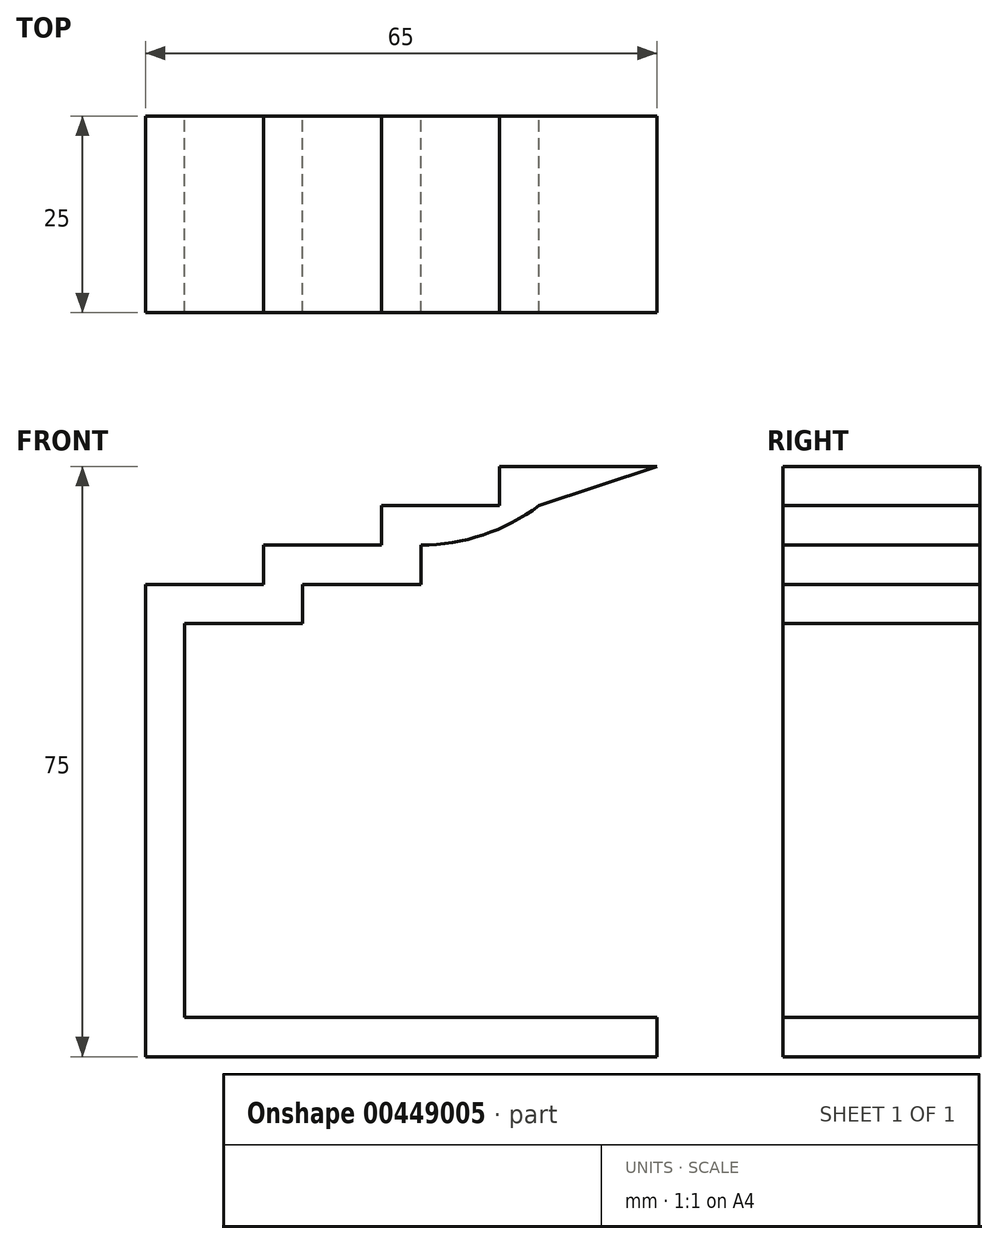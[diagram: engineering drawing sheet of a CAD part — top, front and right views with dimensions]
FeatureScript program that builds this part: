
annotation { "Feature Type Name" : "Feature", "Feature Type Description" : "" }
export const myFeature = defineFeature(function(context is Context, id is Id, definition is map)
    precondition{}
    {
        {
            var Q0;
            Q0=qCreatedBy(makeId("Front.planeOp"),FACE);
            var sketch = newSketch(context, id + "F0", { "sketchPlane" : qUnion([Q0])});
            skLineSegment(sketch, "E0.bottom", {"start": v(0, 0) * mm, "end": v(65, 0) * mm});
            skLineSegment(sketch, "E0.top", {"start": v(0, 5) * mm, "end": v(65, 5) * mm});
            skLineSegment(sketch, "E0.left", {"start": v(0, 0) * mm, "end": v(0, 5) * mm});
            skLineSegment(sketch, "E0.right", {"start": v(65, 0) * mm, "end": v(65, 5) * mm});
            skLineSegment(sketch, "E1.bottom", {"start": v(0, 5) * mm, "end": v(5, 5) * mm});
            skLineSegment(sketch, "E1.top", {"start": v(0, 55) * mm, "end": v(5, 55) * mm});
            skLineSegment(sketch, "E1.left", {"start": v(0, 5) * mm, "end": v(0, 55) * mm});
            skLineSegment(sketch, "E1.right", {"start": v(5, 5) * mm, "end": v(5, 55) * mm});
            skLineSegment(sketch, "E2", {"start": v(0, 55) * mm, "end": v(20, 55) * mm});
            skLineSegment(sketch, "E3", {"start": v(20, 55) * mm, "end": v(20, 60) * mm});
            skLineSegment(sketch, "E4", {"start": v(20, 60) * mm, "end": v(35, 60) * mm});
            skLineSegment(sketch, "E5", {"start": v(35, 60) * mm, "end": v(35, 65) * mm});
            skLineSegment(sketch, "E6", {"start": v(35, 65) * mm, "end": v(50, 65) * mm, "construction": true});
            skLineSegment(sketch, "E7", {"start": v(50, 65) * mm, "end": v(50, 70) * mm, "construction": true});
            skLineSegment(sketch, "E8", {"start": v(50, 70) * mm, "end": v(65, 70) * mm, "construction": true});
            skLineSegment(sketch, "E9", {"start": v(65, 70) * mm, "end": v(65, 75) * mm, "construction": true});
            skLineSegment(sketch, "E10", {"start": v(65, 75) * mm, "end": v(45, 75) * mm});
            skLineSegment(sketch, "E11", {"start": v(45, 75) * mm, "end": v(45, 70) * mm});
            skLineSegment(sketch, "E12", {"start": v(45, 70) * mm, "end": v(30, 70) * mm});
            skLineSegment(sketch, "E13", {"start": v(30, 70) * mm, "end": v(30, 65) * mm});
            skLineSegment(sketch, "E14", {"start": v(30, 65) * mm, "end": v(15, 65) * mm});
            skLineSegment(sketch, "E15", {"start": v(15, 65) * mm, "end": v(15, 60) * mm});
            skLineSegment(sketch, "E16", {"start": v(15, 60) * mm, "end": v(0, 60) * mm});
            skLineSegment(sketch, "E17", {"start": v(0, 60) * mm, "end": v(0, 55) * mm});
            skLineSegment(sketch, "E18", {"start": v(5, 55) * mm, "end": v(20, 55) * mm});
            skLineSegment(sketch, "E19", {"start": v(50, 70) * mm, "end": v(65, 75) * mm});
            skArc(sketch, "E20", {"start": v(35, 65) * mm, "mid": v(42.9, 66.28) * mm, "end": v(50, 70) * mm});
            skSolve(sketch);
        }
        {
            var Q0;
            Q0 = qSketchRegion(id + "F0", true);
            extrude(context, id + "F1", {"entities" : qUnion([Q0]), "depth" : 25 * mm});
        }
    });
